# Revit family: Chair-Soft_Seating-Allermuir-Octo-OCT04
name_source: partatom
category: Furniture
revit_build: Autodesk Revit Architecture 2012 (Build: 20110309_2315(x64)
units: mm (PartAtom-declared; Revit-internal decimal feet)

## types (1)
- OCT04
    04 CSI = 12 51 00
    95 CSI = 12510
    Assembly Code = E2020200
    Base = Metal - Allermuir - Polished Aluminum
    Brochure URL = http://www.allermuir.net
    CAD Blocks URL = http://www.allermuir.net
    Color Availability = See price list for material options
    Cushion = Leather - Allermuir - Fabric - Leather - Brown - Pebble
    Default Elevation = 48 "
    Description = Seat unit
    Fabric Spec Sheets = http://www.allermuir.net
    LEED Stats URL = http://www.allermuir.net
    Manufacturer = Allermuir
    Manufacturer Fax = (419) 887 5805
    Model = OCT04
    Overall Depth = 32 "
    Overall Height = 26 "
    Overall Width = 32 "
    Plastic Arms in Black = No
    Plastic glides = Yes
    Plugin Data URL = http://products.ecoscorecard.com
    Pricing URL = http://www.allermuir.net
    Product Line = Octo
    Product Page URL = http://www.allermuir.net
    Seat Depth = 24 "
    Seat Height = 16 "
    Seat Width = 32 "
    Seat or Top = Leather - Allermuir - Fabric - Leather - Brown - Pebble
    Specifications URL = http://www.allermuir.net
    Stacks = No
    Subcategory = Soft Seating
    Tubular Steel Legs = Yes
    URL = http://www.allermuir.net
    Upholstered Back = Yes
    Upholstered Seat = Yes
    Weight = 0.0 lb
    ecoScorecard Product Page = http://products.ecoscorecard.com
    ecoScorecard_data = http://thesenatorgroup.ecoscorecard.com

## geometry (parser evidence)
native form markers: Blend x13, Sweep x4
no freeform markers — native parametric forms only
